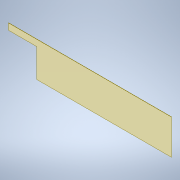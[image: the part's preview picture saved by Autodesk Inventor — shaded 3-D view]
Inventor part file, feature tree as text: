
AUTODESK INVENTOR PART (.ipt)
format: ipt  version: 2021 (Build 250183000, 183)  size: 101,888 bytes
history: native  units: mm
features: extrude x2, sketch x2
ambient origin geometry x8: Origin, YZ Plane, XZ Plane, XY Plane, X Axis, Y Axis, Z Axis, Center Point
bodies: Solid1 (feature_tree)
feature tree (4):
  extrude  "Extrusion1"  Depth=427.0mm
  extrude  "Extrusion2"  Depth=350.0mm
  sketch  "Sketch1"  dims[d0=2000.0mm d1=427.0mm]
  sketch  "Sketch2"  dims[d2=3.0mm d3=0.0mm d4=350.0mm d5=350.0mm d6=10.0mm d7=0.0mm]
